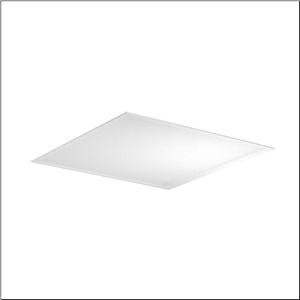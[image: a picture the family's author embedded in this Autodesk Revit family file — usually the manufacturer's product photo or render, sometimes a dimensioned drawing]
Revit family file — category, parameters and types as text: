
# Revit family: apollon_r__31_square_51mp12w72442_a98a
name_source: partatom
category: Lighting Fixtures
units: mm (PartAtom-declared; Revit-internal decimal feet)

## family parameters
Cut with Voids When Loaded = No
Host = Face
Light Source = No
Part Type = Normal
Room Calculation Point = No
Round Connector Dimension = Use Diameter
Shared = No

## types (1)
- Apollon® 31 square (1 x LED, 4000 lm, 27.5 W, 4000K)
    Apparent Load = 28 VA
    CIE Flux Codes = 61 87 97 100 100
    Color Rendering = 80
    Color Temperature = 4000K
    Default Elevation = 1800 mm
    Description = Apollon® 31 square, office luminaire, primary optical cover: micro prismatic cover, of PMMA, CAT 2 (L<= 3000cd/m²), light emission: direct distribution, primary light characteristic: symmetric, installation type: lay-in mounting, LED, rated luminous flux: 4.000lm, luminous efficacy: 145lm/W, light colour: 840, colour temperature: 4000K, with terminal, 3-pole, mains connection: 220..240V, AC, 50/60Hz, rated input power: 28W, housing, of aluminium, traffic white (RAL 9016), module: M600, length: 595mm, width: 595mm, height: 32mm, housing upper side, of sheet steel, galvanised, protection rating (complete): IP20, protection rating (on room side): IP40, insulation class (complete): insulation class II (safety insulation), certification: CE, ENEC, impact resistance: IK03, permissible operating ambient temperature: -20..+40°C, permissible storage temperature: -20..+60°C, packaging unit: 1 piece
    Height = 0 mm  [stored 0 ft]
    Lamp = 1 x LED
    Lamp Light Flux = 4000 lm
    Lamp Power = 27.5 W
    Lamp count = 1
    Length = 595 mm
    Luminous efficacy = 145 lm/W
    Manufacturer = Siteco
    ModVariant = No
    Model = 51MP12W72442
    Mounting Place = Ceiling
    Mounting Type = Recessed
    Number of Poles = 1
    OnlyDefault = Yes
    Power Factor = 1
    Product Name = Apollon® 31 square
    Product group = office luminaire | ceiling recessed
    ProductGroupID = 400
    Protection Class = Protection class II
    Protection Degree = IP 20
    RLX_Detail_Level = 1
    RLX_Emergency_Light_Flux = 0 lm
    RLX_Emergency_Type = 0
    RLX_Emergency_Type_DB = No
    RlxData = <blob elided: 12481 chars, md5=a648696e>
    Socket = socket
    Standby Power = 0 W
    System Light Flux = 4000 lm
    System Power = 28 W
    Type Comments = Product without accessories
    Type Image = l_1291035.jpg
    URL = http://relux.com
    VarID = ---
    Voltage = 0 V
    Weight = 0.00 kg
    Width = 595 mm

note: [stored X ft] marks values corroborated as IEEE doubles in the binary element streams (Revit-internal decimal feet)

## geometry (parser evidence)
native form markers: Sweep x9
no freeform markers — native parametric forms only
